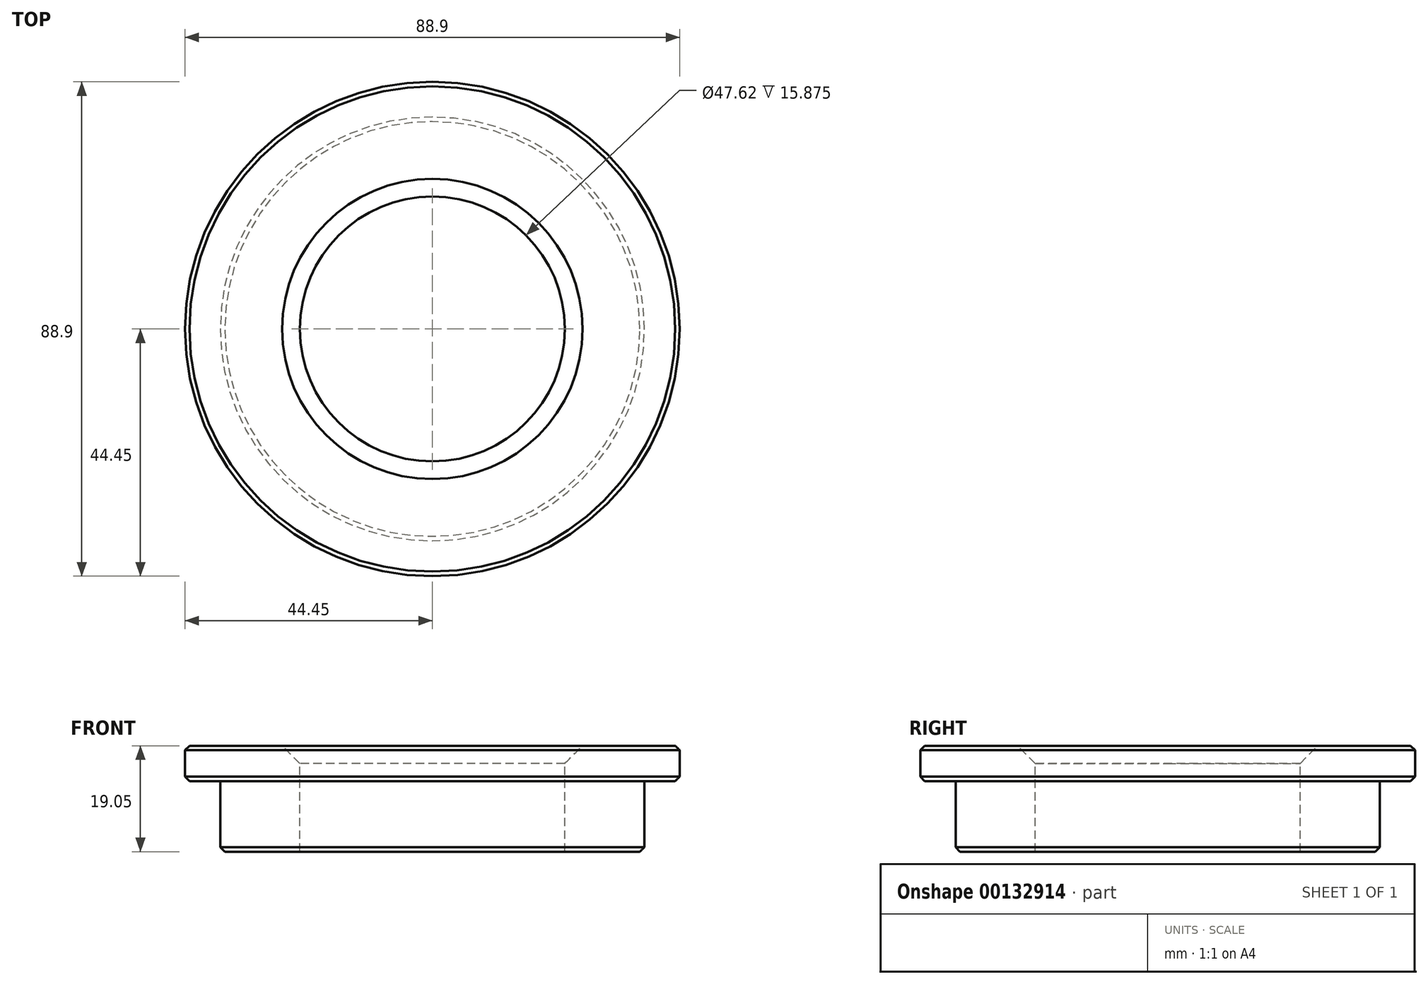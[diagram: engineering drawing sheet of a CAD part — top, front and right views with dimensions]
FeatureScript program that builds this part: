
annotation { "Feature Type Name" : "Feature", "Feature Type Description" : "" }
export const myFeature = defineFeature(function(context is Context, id is Id, definition is map)
    precondition{}
    {
        {
            var Q0;
            Q0=qCreatedBy(makeId("Top.planeOp"),FACE);
            var sketch = newSketch(context, id + "F0", { "sketchPlane" : qUnion([Q0])});
            skCircle(sketch, "E0", {"center": v(0, 0) * mm, "radius": 23.81 * mm});
            skCircle(sketch, "E1", {"center": v(0, 0) * mm, "radius": 38.1 * mm});
            skCircle(sketch, "E2", {"center": v(0, 0) * mm, "radius": 44.45 * mm});
            skSolve(sketch);
        }
        {
            var Q0;
            Q0=makeQuery(id+"F0.imprint","IMPRINT",FACE,{"disambiguationData":[TD([[makeQuery(id+"F0.imprint","IMPRINT",EDGE,{"derivedFrom":sQuery(id+"F0.wireOp",EDGE,"E0")}),-1.0]])]});
            extrude(context, id + "F1", {"entities" : qUnion([Q0]), "oppositeDirection" : true, "depth" : 12.7 * mm});
        }
        {
            var Q0;
            Q0 = qSketchRegion(id + "F0", true);
            var Q1;
            Q1=makeQuery(id+"F1.opExtrude","CAP_FACE",FACE,{"disambiguationData":[OSD([sQuery(id+"F0.wireOp",EDGE,"E0"),sQuery(id+"F0.wireOp",EDGE,"E1")])],"isStart":true});
            extrude(context, id + "F2", {"entities" : qUnion([Q0, Q1]), "operationType" : NewBodyOperationType.ADD, "depth" : 6.35 * mm});
        }
        {
            var Q0;
            Q0=makeQuery(id+"F2.opExtrude","CAP_EDGE",EDGE,{"disambiguationData":[OSD([sQuery(id+"F0.wireOp",EDGE,"E0")])],"isStart":false});
            chamfer(context, id + "F3", {"entities" : qUnion([Q0]), "width" : 3.17 * mm, "tangentPropagation" : true});
        }
        {
            var Q0;
            Q0=makeQuery(id+"F2.opExtrude","CAP_EDGE",EDGE,{"disambiguationData":[OSD([sQuery(id+"F0.wireOp",EDGE,"E2")])],"isStart":false});
            var Q1;
            Q1=makeQuery(id+"F2.opExtrude","CAP_EDGE",EDGE,{"disambiguationData":[OSD([sQuery(id+"F0.wireOp",EDGE,"E2")])],"isStart":true});
            var Q2;
            Q2=makeQuery(id+"F1.opExtrude","CAP_EDGE",EDGE,{"disambiguationData":[OSD([sQuery(id+"F0.wireOp",EDGE,"E1")])],"isStart":false});
            chamfer(context, id + "F4", {"entities" : qUnion([Q0, Q1, Q2]), "width" : 0.81 * mm, "tangentPropagation" : true});
        }
    });
